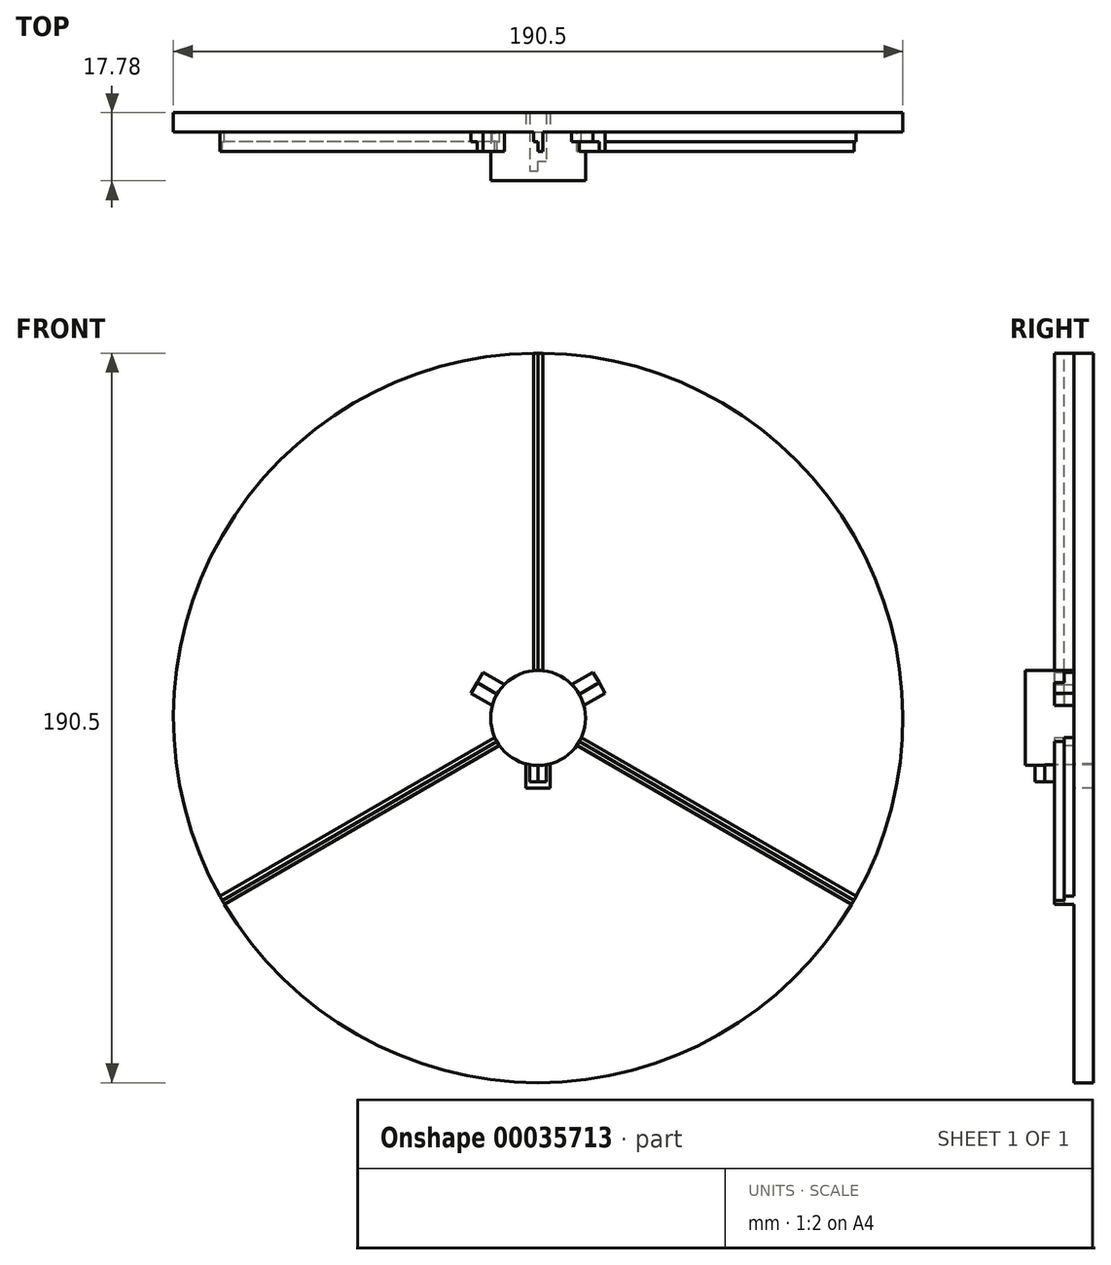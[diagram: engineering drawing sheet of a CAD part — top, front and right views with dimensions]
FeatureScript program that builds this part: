
annotation { "Feature Type Name" : "Feature", "Feature Type Description" : "" }
export const myFeature = defineFeature(function(context is Context, id is Id, definition is map)
    precondition{}
    {
        {
            var Q0;
            Q0=qCreatedBy(makeId("Front.planeOp"),FACE);
            var sketch = newSketch(context, id + "F0", { "sketchPlane" : qUnion([Q0])});
            skLineSegment(sketch, "E0.MirrorCS", {"start": v(1.2, 0) * mm, "end": v(1.2, 95.24) * mm});
            skLineSegment(sketch, "E1", {"start": v(0, 0) * mm, "end": v(-82.49, 47.62) * mm});
            skLineSegment(sketch, "E2", {"start": v(0, 0) * mm, "end": v(82.49, 47.62) * mm});
            skCircle(sketch, "E3", {"center": v(0, 0) * mm, "radius": 95.25 * mm});
            skLineSegment(sketch, "E4", {"start": v(0, 97.8) * mm, "end": v(-97.8, 97.8) * mm});
            skLineSegment(sketch, "E5", {"start": v(-97.8, -97.8) * mm, "end": v(0, -97.8) * mm});
            skLineSegment(sketch, "E6", {"start": v(-97.8, 97.8) * mm, "end": v(-97.8, -97.8) * mm});
            skLineSegment(sketch, "E7", {"start": v(0.6, 1.03) * mm, "end": v(83.08, -46.6) * mm});
            skLineSegment(sketch, "E8.MirrorCS", {"start": v(-0.6, -1.03) * mm, "end": v(81.89, -48.65) * mm});
            skLineSegment(sketch, "E9.MirrorCS", {"start": v(0, 97.8) * mm, "end": v(97.8, 97.8) * mm});
            skLineSegment(sketch, "E10.MirrorCS", {"start": v(97.8, -97.8) * mm, "end": v(0, -97.8) * mm});
            skLineSegment(sketch, "E11", {"start": v(-1.2, 0) * mm, "end": v(-1.2, 95.24) * mm});
            skLineSegment(sketch, "E12.MirrorCS", {"start": v(0, 0) * mm, "end": v(-82.49, -47.62) * mm});
            skLineSegment(sketch, "E13.MirrorCS", {"start": v(97.8, 97.8) * mm, "end": v(97.8, -97.8) * mm});
            skLineSegment(sketch, "E14.MirrorCS", {"start": v(-0.6, 1.03) * mm, "end": v(-83.08, -46.6) * mm});
            skLineSegment(sketch, "E15", {"start": v(0, 0) * mm, "end": v(0, -95.25) * mm});
            skLineSegment(sketch, "E16", {"start": v(0, 0) * mm, "end": v(0, 95.25) * mm});
            skLineSegment(sketch, "E17", {"start": v(0, 0) * mm, "end": v(82.49, -47.62) * mm});
            skLineSegment(sketch, "E18.MirrorCS", {"start": v(0.6, -1.03) * mm, "end": v(-81.89, -48.65) * mm});
            skCircle(sketch, "E19", {"center": v(0, 0) * mm, "radius": 12.4 * mm});
            skCircle(sketch, "E20", {"center": v(0, -15.21) * mm, "radius": 2.82 * mm, "construction": true});
            skLineSegment(sketch, "E21.MirrorCS", {"start": v(2.17, 0) * mm, "end": v(2.17, -14.57) * mm});
            skCircle(sketch, "E22", {"center": v(0, -14.57) * mm, "radius": 2.17 * mm, "construction": true});
            skLineSegment(sketch, "E23.MirrorCS", {"start": v(2.82, 0) * mm, "end": v(2.82, -15.21) * mm});
            skLineSegment(sketch, "E24", {"start": v(-2.17, 0) * mm, "end": v(-2.17, -14.57) * mm});
            skLineSegment(sketch, "E25", {"start": v(-2.82, 0) * mm, "end": v(-2.82, -15.21) * mm});
            skCircle(sketch, "E26", {"center": v(0, 0) * mm, "radius": 1.2 * mm, "construction": true});
            skLineSegment(sketch, "E27", {"start": v(-1.2, 0) * mm, "end": v(0, 0) * mm, "construction": true});
            skLineSegment(sketch, "E28", {"start": v(1.2, 0) * mm, "end": v(0, 0) * mm, "construction": true});
            skLineSegment(sketch, "E29.MirrorCS", {"start": v(-0.6, -1.03) * mm, "end": v(0, 0) * mm, "construction": true});
            skLineSegment(sketch, "E30.MirrorCS", {"start": v(0.6, 1.03) * mm, "end": v(0, 0) * mm, "construction": true});
            skLineSegment(sketch, "E31.MirrorCS", {"start": v(-0.6, 1.03) * mm, "end": v(0, 0) * mm, "construction": true});
            skLineSegment(sketch, "E32.MirrorCS", {"start": v(0.6, -1.03) * mm, "end": v(0, 0) * mm, "construction": true});
            skLineSegment(sketch, "E33", {"start": v(-2.82, 0) * mm, "end": v(0, 0) * mm, "construction": true});
            skLineSegment(sketch, "E34", {"start": v(0, 0) * mm, "end": v(2.82, 0) * mm, "construction": true});
            skLineSegment(sketch, "E35", {"start": v(-2.82, -15.21) * mm, "end": v(-2.82, -18.03) * mm});
            skLineSegment(sketch, "E36", {"start": v(-2.82, -18.03) * mm, "end": v(0, -18.03) * mm});
            skLineSegment(sketch, "E37", {"start": v(0, -18.03) * mm, "end": v(2.82, -18.03) * mm});
            skLineSegment(sketch, "E38", {"start": v(2.82, -18.03) * mm, "end": v(2.82, -15.21) * mm});
            skLineSegment(sketch, "E39", {"start": v(-2.17, -14.57) * mm, "end": v(-2.17, -16.74) * mm});
            skLineSegment(sketch, "E40", {"start": v(-2.17, -16.74) * mm, "end": v(0, -16.74) * mm});
            skLineSegment(sketch, "E41", {"start": v(0, -16.74) * mm, "end": v(2.17, -16.74) * mm});
            skLineSegment(sketch, "E42", {"start": v(2.17, -16.74) * mm, "end": v(2.17, -14.57) * mm});
            skCircle(sketch, "E43", {"center": v(-10.73, 6.2) * mm, "radius": 3.18 * mm, "construction": true});
            skCircle(sketch, "E44", {"center": v(0, -12.4) * mm, "radius": 3.18 * mm, "construction": true});
            skCircle(sketch, "E45", {"center": v(10.73, 6.2) * mm, "radius": 3.18 * mm, "construction": true});
            skLineSegment(sketch, "E46", {"start": v(-2.82, 0) * mm, "end": v(-3.18, 0) * mm, "construction": true});
            skLineSegment(sketch, "E47", {"start": v(-3.18, 0) * mm, "end": v(-3.18, -12.4) * mm});
            skLineSegment(sketch, "E48", {"start": v(-3.18, -12.4) * mm, "end": v(-3.18, -18.39) * mm});
            skLineSegment(sketch, "E49", {"start": v(-3.18, -18.39) * mm, "end": v(0, -18.39) * mm});
            skCircle(sketch, "E50", {"center": v(-2.82, -18.03) * mm, "radius": 0.36 * mm, "construction": true});
            skLineSegment(sketch, "E51.MirrorCS", {"start": v(2.82, 0) * mm, "end": v(3.17, 0) * mm});
            skLineSegment(sketch, "E52.MirrorCS", {"start": v(3.17, 0) * mm, "end": v(3.17, -12.4) * mm});
            skLineSegment(sketch, "E53.MirrorCS", {"start": v(3.17, -18.39) * mm, "end": v(0, -18.39) * mm});
            skLineSegment(sketch, "E54.MirrorCS", {"start": v(3.17, -12.4) * mm, "end": v(3.17, -18.39) * mm});
            skLineSegment(sketch, "E55.MirrorCS", {"start": v(1.4, -2.44) * mm, "end": v(1.59, -2.75) * mm, "construction": true});
            skLineSegment(sketch, "E56.MirrorCS", {"start": v(-1.4, 2.44) * mm, "end": v(-1.59, 2.75) * mm, "construction": true});
            skLineSegment(sketch, "E57.MirrorCS", {"start": v(-1.59, 2.75) * mm, "end": v(9.15, 8.95) * mm});
            skLineSegment(sketch, "E58.MirrorCS", {"start": v(1.59, -2.75) * mm, "end": v(12.32, 3.45) * mm});
            skLineSegment(sketch, "E59.MirrorCS", {"start": v(0, 0) * mm, "end": v(1.4, -2.44) * mm, "construction": true});
            skLineSegment(sketch, "E60.MirrorCS", {"start": v(-1.4, 2.44) * mm, "end": v(0, 0) * mm, "construction": true});
            skLineSegment(sketch, "E61.MirrorCS", {"start": v(9.15, 8.95) * mm, "end": v(14.34, 11.94) * mm});
            skLineSegment(sketch, "E62.MirrorCS", {"start": v(14.34, 11.94) * mm, "end": v(15.93, 9.2) * mm});
            skLineSegment(sketch, "E63.MirrorCS", {"start": v(12.32, 3.45) * mm, "end": v(17.51, 6.45) * mm});
            skLineSegment(sketch, "E64.MirrorCS", {"start": v(17.51, 6.45) * mm, "end": v(15.93, 9.2) * mm});
            skLineSegment(sketch, "E65.MirrorCS", {"start": v(1.4, 2.44) * mm, "end": v(1.59, 2.75) * mm, "construction": true});
            skLineSegment(sketch, "E66.MirrorCS", {"start": v(1.4, 2.44) * mm, "end": v(0, 0) * mm, "construction": true});
            skLineSegment(sketch, "E67.MirrorCS", {"start": v(1.59, 2.75) * mm, "end": v(-9.15, 8.95) * mm});
            skLineSegment(sketch, "E68.MirrorCS", {"start": v(0, 0) * mm, "end": v(-1.4, -2.44) * mm, "construction": true});
            skLineSegment(sketch, "E69.MirrorCS", {"start": v(-1.4, -2.44) * mm, "end": v(-1.59, -2.75) * mm, "construction": true});
            skLineSegment(sketch, "E70.MirrorCS", {"start": v(-1.59, -2.75) * mm, "end": v(-12.32, 3.45) * mm});
            skLineSegment(sketch, "E71.MirrorCS", {"start": v(-9.15, 8.95) * mm, "end": v(-14.34, 11.94) * mm});
            skLineSegment(sketch, "E72.MirrorCS", {"start": v(-14.34, 11.94) * mm, "end": v(-15.93, 9.2) * mm});
            skLineSegment(sketch, "E73.MirrorCS", {"start": v(-17.51, 6.45) * mm, "end": v(-15.93, 9.2) * mm});
            skLineSegment(sketch, "E74.MirrorCS", {"start": v(-12.32, 3.45) * mm, "end": v(-17.51, 6.45) * mm});
            skSolve(sketch);
        }
        {
            var Q0;
            {var subQ6=sQuery(id+"F0.wireOp",EDGE,"E61.MirrorCS");Q0=makeQuery(id+"F0.imprint","IMPRINT",FACE,{"disambiguationData":[TD([[makeQuery(id+"F0.imprint","IMPRINT",EDGE,{"derivedFrom":subQ6}),1.0]])]});}
            var Q1;
            {var subQ0=sQuery(id+"F0.wireOp",EDGE,"E71.MirrorCS");Q1=makeQuery(id+"F0.imprint","IMPRINT",FACE,{"disambiguationData":[TD([[makeQuery(id+"F0.imprint","IMPRINT",EDGE,{"derivedFrom":subQ0}),-1.0]])]});}
            var Q2;
            {var subQ1=sQuery(id+"F0.wireOp",EDGE,"E53.MirrorCS");Q2=makeQuery(id+"F0.imprint","IMPRINT",FACE,{"disambiguationData":[TD([[makeQuery(id+"F0.imprint","IMPRINT",EDGE,{"derivedFrom":subQ1}),1.0]])]});}
            var Q3;
            {var subQ0=sQuery(id+"F0.wireOp",EDGE,"E73.MirrorCS");Q3=makeQuery(id+"F0.imprint","IMPRINT",FACE,{"disambiguationData":[TD([[makeQuery(id+"F0.imprint","IMPRINT",EDGE,{"derivedFrom":subQ0}),1.0]])]});}
            var Q4;
            {var subQ1=sQuery(id+"F0.wireOp",EDGE,"E63.MirrorCS");Q4=makeQuery(id+"F0.imprint","IMPRINT",FACE,{"disambiguationData":[TD([[makeQuery(id+"F0.imprint","IMPRINT",EDGE,{"derivedFrom":subQ1}),-1.0]])]});}
            var Q5;
            {var subQ1=sQuery(id+"F0.wireOp",EDGE,"E48");Q5=makeQuery(id+"F0.imprint","IMPRINT",FACE,{"disambiguationData":[TD([[makeQuery(id+"F0.imprint","IMPRINT",EDGE,{"derivedFrom":subQ1}),-1.0]])]});}
            var Q6;
            Q6=makeQuery(id+"F0.imprint","IMPRINT",FACE,{"disambiguationData":[TD([[makeQuery(id+"F0.imprint","IMPRINT",EDGE,{"derivedFrom":sQuery(id+"F0.wireOp",EDGE,"E4")}),1.0]])]});
            var Q7;
            {var subQ3=sQuery(id+"F0.wireOp",EDGE,"E0.MirrorCS");var subQ5=sQuery(id+"F0.wireOp",EDGE,"E3");var subQ7=makeQuery(id+"F0.imprint","INTERSECT",VERTEX,{"derivedFrom":[subQ3,subQ5]});Q7=makeQuery(id+"F0.imprint","IMPRINT",FACE,{"disambiguationData":[TD([[makeQuery(id+"F0.imprint","IMPRINT",EDGE,{"disambiguationData":[TD([[subQ7,1.0]])],"derivedFrom":subQ3}),1.0]])]});}
            var Q8;
            {var subQ3=sQuery(id+"F0.wireOp",EDGE,"E8.MirrorCS");var subQ5=sQuery(id+"F0.wireOp",EDGE,"E3");var subQ7=makeQuery(id+"F0.imprint","INTERSECT",VERTEX,{"derivedFrom":[subQ5,subQ3]});Q8=makeQuery(id+"F0.imprint","IMPRINT",FACE,{"disambiguationData":[TD([[makeQuery(id+"F0.imprint","IMPRINT",EDGE,{"disambiguationData":[TD([[subQ7,-1.0]])],"derivedFrom":subQ5}),1.0]])]});}
            var Q9;
            {var subQ3=sQuery(id+"F0.wireOp",EDGE,"E3");var subQ5=sQuery(id+"F0.wireOp",EDGE,"E12.MirrorCS");var subQ7=makeQuery(id+"F0.imprint","INTERSECT",VERTEX,{"derivedFrom":[subQ3,subQ5]});Q9=makeQuery(id+"F0.imprint","IMPRINT",FACE,{"disambiguationData":[TD([[makeQuery(id+"F0.imprint","IMPRINT",EDGE,{"disambiguationData":[TD([[subQ7,-1.0]])],"derivedFrom":subQ3}),1.0]])]});}
            var Q10;
            {var subQ3=sQuery(id+"F0.wireOp",EDGE,"E11");var subQ5=sQuery(id+"F0.wireOp",EDGE,"E3");var subQ7=makeQuery(id+"F0.imprint","INTERSECT",VERTEX,{"derivedFrom":[subQ5,subQ3]});Q10=makeQuery(id+"F0.imprint","IMPRINT",FACE,{"disambiguationData":[TD([[makeQuery(id+"F0.imprint","IMPRINT",EDGE,{"disambiguationData":[TD([[subQ7,1.0]])],"derivedFrom":subQ5}),1.0]])]});}
            var Q11;
            {var subQ3=sQuery(id+"F0.wireOp",EDGE,"E12.MirrorCS");var subQ5=sQuery(id+"F0.wireOp",EDGE,"E3");var subQ7=makeQuery(id+"F0.imprint","INTERSECT",VERTEX,{"derivedFrom":[subQ5,subQ3]});Q11=makeQuery(id+"F0.imprint","IMPRINT",FACE,{"disambiguationData":[TD([[makeQuery(id+"F0.imprint","IMPRINT",EDGE,{"disambiguationData":[TD([[subQ7,1.0]])],"derivedFrom":subQ5}),1.0]])]});}
            var Q12;
            {var subQ3=sQuery(id+"F0.wireOp",EDGE,"E7");var subQ5=sQuery(id+"F0.wireOp",EDGE,"E3");var subQ7=makeQuery(id+"F0.imprint","INTERSECT",VERTEX,{"derivedFrom":[subQ5,subQ3]});Q12=makeQuery(id+"F0.imprint","IMPRINT",FACE,{"disambiguationData":[TD([[makeQuery(id+"F0.imprint","IMPRINT",EDGE,{"disambiguationData":[TD([[subQ7,1.0]])],"derivedFrom":subQ5}),1.0]])]});}
            var Q13;
            {var subQ0=sQuery(id+"F0.wireOp",EDGE,"E57.MirrorCS");var subQ3=sQuery(id+"F0.wireOp",EDGE,"E0.MirrorCS");var subQ4=makeQuery(id+"F0.imprint","INTERSECT",VERTEX,{"derivedFrom":[subQ3,subQ0]});Q13=makeQuery(id+"F0.imprint","IMPRINT",FACE,{"disambiguationData":[TD([[makeQuery(id+"F0.imprint","IMPRINT",EDGE,{"disambiguationData":[TD([[subQ4,-1.0]])],"derivedFrom":subQ3}),-1.0]])]});}
            var Q14;
            {var subQ0=sQuery(id+"F0.wireOp",EDGE,"E67.MirrorCS");var subQ3=sQuery(id+"F0.wireOp",EDGE,"E11");var subQ4=makeQuery(id+"F0.imprint","INTERSECT",VERTEX,{"derivedFrom":[subQ3,subQ0]});Q14=makeQuery(id+"F0.imprint","IMPRINT",FACE,{"disambiguationData":[TD([[makeQuery(id+"F0.imprint","IMPRINT",EDGE,{"disambiguationData":[TD([[subQ4,-1.0]])],"derivedFrom":subQ3}),1.0]])]});}
            var Q15;
            {var subQ0=sQuery(id+"F0.wireOp",EDGE,"E57.MirrorCS");var subQ3=sQuery(id+"F0.wireOp",EDGE,"E0.MirrorCS");var subQ4=makeQuery(id+"F0.imprint","INTERSECT",VERTEX,{"derivedFrom":[subQ3,subQ0]});Q15=makeQuery(id+"F0.imprint","IMPRINT",FACE,{"disambiguationData":[TD([[makeQuery(id+"F0.imprint","IMPRINT",EDGE,{"disambiguationData":[TD([[subQ4,-1.0]])],"derivedFrom":subQ3}),1.0]])]});}
            var Q16;
            {var subQ0=sQuery(id+"F0.wireOp",EDGE,"E47");var subQ3=sQuery(id+"F0.wireOp",EDGE,"E18.MirrorCS");var subQ4=makeQuery(id+"F0.imprint","INTERSECT",VERTEX,{"derivedFrom":[subQ3,subQ0]});Q16=makeQuery(id+"F0.imprint","IMPRINT",FACE,{"disambiguationData":[TD([[makeQuery(id+"F0.imprint","IMPRINT",EDGE,{"disambiguationData":[TD([[subQ4,-1.0]])],"derivedFrom":subQ3}),1.0]])]});}
            var Q17;
            {var subQ6=sQuery(id+"F0.wireOp",EDGE,"E61.MirrorCS");Q17=makeQuery(id+"F0.imprint","IMPRINT",FACE,{"disambiguationData":[TD([[makeQuery(id+"F0.imprint","IMPRINT",EDGE,{"derivedFrom":subQ6}),-1.0]])]});}
            var Q18;
            {var subQ1=sQuery(id+"F0.wireOp",EDGE,"E52.MirrorCS");var subQ3=sQuery(id+"F0.wireOp",EDGE,"E8.MirrorCS");var subQ5=makeQuery(id+"F0.imprint","INTERSECT",VERTEX,{"derivedFrom":[subQ3,subQ1]});Q18=makeQuery(id+"F0.imprint","IMPRINT",FACE,{"disambiguationData":[TD([[makeQuery(id+"F0.imprint","IMPRINT",EDGE,{"disambiguationData":[TD([[subQ5,-1.0]])],"derivedFrom":subQ3}),-1.0]])]});}
            var Q19;
            {var subQ6=sQuery(id+"F0.wireOp",EDGE,"E71.MirrorCS");Q19=makeQuery(id+"F0.imprint","IMPRINT",FACE,{"disambiguationData":[TD([[makeQuery(id+"F0.imprint","IMPRINT",EDGE,{"derivedFrom":subQ6}),1.0]])]});}
            var Q20;
            {var subQ0=sQuery(id+"F0.wireOp",EDGE,"E67.MirrorCS");var subQ3=sQuery(id+"F0.wireOp",EDGE,"E11");var subQ4=makeQuery(id+"F0.imprint","INTERSECT",VERTEX,{"derivedFrom":[subQ3,subQ0]});Q20=makeQuery(id+"F0.imprint","IMPRINT",FACE,{"disambiguationData":[TD([[makeQuery(id+"F0.imprint","IMPRINT",EDGE,{"disambiguationData":[TD([[subQ4,-1.0]])],"derivedFrom":subQ3}),-1.0]])]});}
            var Q21;
            {var subQ0=sQuery(id+"F0.wireOp",EDGE,"E58.MirrorCS");var subQ3=sQuery(id+"F0.wireOp",EDGE,"E7");var subQ4=makeQuery(id+"F0.imprint","INTERSECT",VERTEX,{"derivedFrom":[subQ3,subQ0]});Q21=makeQuery(id+"F0.imprint","IMPRINT",FACE,{"disambiguationData":[TD([[makeQuery(id+"F0.imprint","IMPRINT",EDGE,{"disambiguationData":[TD([[subQ4,-1.0]])],"derivedFrom":subQ3}),-1.0]])]});}
            var Q22;
            {var subQ3=sQuery(id+"F0.wireOp",EDGE,"E11");var subQ8=makeQuery(id+"F0.imprint","INTERSECT",VERTEX,{"derivedFrom":[subQ3,sQuery(id+"F0.wireOp",EDGE,"E57.MirrorCS")]});Q22=makeQuery(id+"F0.imprint","IMPRINT",FACE,{"disambiguationData":[TD([[makeQuery(id+"F0.imprint","IMPRINT",EDGE,{"disambiguationData":[TD([[subQ8,-1.0]])],"derivedFrom":subQ3}),1.0]])]});}
            var Q23;
            {var subQ3=sQuery(id+"F0.wireOp",EDGE,"E18.MirrorCS");var subQ7=makeQuery(id+"F0.imprint","INTERSECT",VERTEX,{"derivedFrom":[subQ3,sQuery(id+"F0.wireOp",EDGE,"E70.MirrorCS")]});Q23=makeQuery(id+"F0.imprint","IMPRINT",FACE,{"disambiguationData":[TD([[makeQuery(id+"F0.imprint","IMPRINT",EDGE,{"disambiguationData":[TD([[subQ7,-1.0]])],"derivedFrom":subQ3}),1.0]])]});}
            var Q24;
            {var subQ3=sQuery(id+"F0.wireOp",EDGE,"E73.MirrorCS");Q24=makeQuery(id+"F0.imprint","IMPRINT",FACE,{"disambiguationData":[TD([[makeQuery(id+"F0.imprint","IMPRINT",EDGE,{"derivedFrom":subQ3}),-1.0]])]});}
            var Q25;
            {var subQ3=sQuery(id+"F0.wireOp",EDGE,"E0.MirrorCS");var subQ5=makeQuery(id+"F0.imprint","INTERSECT",VERTEX,{"derivedFrom":[subQ3,sQuery(id+"F0.wireOp",EDGE,"E67.MirrorCS")]});Q25=makeQuery(id+"F0.imprint","IMPRINT",FACE,{"disambiguationData":[TD([[makeQuery(id+"F0.imprint","IMPRINT",EDGE,{"disambiguationData":[TD([[subQ5,-1.0]])],"derivedFrom":subQ3}),-1.0]])]});}
            var Q26;
            {var subQ3=sQuery(id+"F0.wireOp",EDGE,"E8.MirrorCS");var subQ5=sQuery(id+"F0.wireOp",EDGE,"E52.MirrorCS");var subQ7=makeQuery(id+"F0.imprint","INTERSECT",VERTEX,{"derivedFrom":[subQ3,subQ5]});Q26=makeQuery(id+"F0.imprint","IMPRINT",FACE,{"disambiguationData":[TD([[makeQuery(id+"F0.imprint","IMPRINT",EDGE,{"disambiguationData":[TD([[subQ7,-1.0]])],"derivedFrom":subQ3}),1.0]])]});}
            var Q27;
            {var subQ3=sQuery(id+"F0.wireOp",EDGE,"E14.MirrorCS");var subQ8=makeQuery(id+"F0.imprint","INTERSECT",VERTEX,{"derivedFrom":[subQ3,sQuery(id+"F0.wireOp",EDGE,"E25")]});Q27=makeQuery(id+"F0.imprint","IMPRINT",FACE,{"disambiguationData":[TD([[makeQuery(id+"F0.imprint","IMPRINT",EDGE,{"disambiguationData":[TD([[subQ8,-1.0]])],"derivedFrom":subQ3}),-1.0]])]});}
            var Q28;
            {var subQ6=sQuery(id+"F0.wireOp",EDGE,"E63.MirrorCS");Q28=makeQuery(id+"F0.imprint","IMPRINT",FACE,{"disambiguationData":[TD([[makeQuery(id+"F0.imprint","IMPRINT",EDGE,{"derivedFrom":subQ6}),1.0]])]});}
            var Q29;
            {var subQ0=sQuery(id+"F0.wireOp",EDGE,"E67.MirrorCS");var subQ3=sQuery(id+"F0.wireOp",EDGE,"E0.MirrorCS");var subQ4=makeQuery(id+"F0.imprint","INTERSECT",VERTEX,{"derivedFrom":[subQ3,subQ0]});Q29=makeQuery(id+"F0.imprint","IMPRINT",FACE,{"disambiguationData":[TD([[makeQuery(id+"F0.imprint","IMPRINT",EDGE,{"disambiguationData":[TD([[subQ4,-1.0]])],"derivedFrom":subQ3}),1.0]])]});}
            var Q30;
            {var subQ0=sQuery(id+"F0.wireOp",EDGE,"E23.MirrorCS");var subQ3=sQuery(id+"F0.wireOp",EDGE,"E8.MirrorCS");var subQ4=makeQuery(id+"F0.imprint","INTERSECT",VERTEX,{"derivedFrom":[subQ3,subQ0]});Q30=makeQuery(id+"F0.imprint","IMPRINT",FACE,{"disambiguationData":[TD([[makeQuery(id+"F0.imprint","IMPRINT",EDGE,{"disambiguationData":[TD([[subQ4,-1.0]])],"derivedFrom":subQ3}),-1.0]])]});}
            var Q31;
            {var subQ0=sQuery(id+"F0.wireOp",EDGE,"E24");var subQ3=sQuery(id+"F0.wireOp",EDGE,"E18.MirrorCS");var subQ4=makeQuery(id+"F0.imprint","INTERSECT",VERTEX,{"derivedFrom":[subQ3,subQ0]});Q31=makeQuery(id+"F0.imprint","IMPRINT",FACE,{"disambiguationData":[TD([[makeQuery(id+"F0.imprint","IMPRINT",EDGE,{"disambiguationData":[TD([[subQ4,-1.0]])],"derivedFrom":subQ3}),1.0]])]});}
            var Q32;
            {var subQ3=sQuery(id+"F0.wireOp",EDGE,"E18.MirrorCS");var subQ5=sQuery(id+"F0.wireOp",EDGE,"E25");var subQ7=makeQuery(id+"F0.imprint","INTERSECT",VERTEX,{"derivedFrom":[subQ3,subQ5]});Q32=makeQuery(id+"F0.imprint","IMPRINT",FACE,{"disambiguationData":[TD([[makeQuery(id+"F0.imprint","IMPRINT",EDGE,{"disambiguationData":[TD([[subQ7,-1.0]])],"derivedFrom":subQ3}),1.0]])]});}
            var Q33;
            {var subQ3=sQuery(id+"F0.wireOp",EDGE,"E8.MirrorCS");var subQ5=sQuery(id+"F0.wireOp",EDGE,"E21.MirrorCS");var subQ7=makeQuery(id+"F0.imprint","INTERSECT",VERTEX,{"derivedFrom":[subQ3,subQ5]});Q33=makeQuery(id+"F0.imprint","IMPRINT",FACE,{"disambiguationData":[TD([[makeQuery(id+"F0.imprint","IMPRINT",EDGE,{"disambiguationData":[TD([[subQ7,-1.0]])],"derivedFrom":subQ3}),-1.0]])]});}
            var Q34;
            {var subQ0=sQuery(id+"F0.wireOp",EDGE,"E70.MirrorCS");var subQ3=sQuery(id+"F0.wireOp",EDGE,"E14.MirrorCS");var subQ4=makeQuery(id+"F0.imprint","INTERSECT",VERTEX,{"derivedFrom":[subQ3,subQ0]});Q34=makeQuery(id+"F0.imprint","IMPRINT",FACE,{"disambiguationData":[TD([[makeQuery(id+"F0.imprint","IMPRINT",EDGE,{"disambiguationData":[TD([[subQ4,-1.0]])],"derivedFrom":subQ3}),-1.0]])]});}
            var Q35;
            {var subQ3=sQuery(id+"F0.wireOp",EDGE,"E8.MirrorCS");var subQ5=makeQuery(id+"F0.imprint","INTERSECT",VERTEX,{"derivedFrom":[subQ3,sQuery(id+"F0.wireOp",EDGE,"E58.MirrorCS")]});Q35=makeQuery(id+"F0.imprint","IMPRINT",FACE,{"disambiguationData":[TD([[makeQuery(id+"F0.imprint","IMPRINT",EDGE,{"disambiguationData":[TD([[subQ5,-1.0]])],"derivedFrom":subQ3}),-1.0]])]});}
            var Q36;
            {var subQ1=sQuery(id+"F0.wireOp",EDGE,"E14.MirrorCS");var subQ5=sQuery(id+"F0.wireOp",EDGE,"E70.MirrorCS");var subQ6=makeQuery(id+"F0.imprint","INTERSECT",VERTEX,{"derivedFrom":[subQ1,subQ5]});Q36=makeQuery(id+"F0.imprint","IMPRINT",FACE,{"disambiguationData":[TD([[makeQuery(id+"F0.imprint","IMPRINT",EDGE,{"disambiguationData":[TD([[subQ6,-1.0]])],"derivedFrom":subQ1}),1.0]])]});}
            var Q37;
            {var subQ4=sQuery(id+"F0.wireOp",EDGE,"E41");Q37=makeQuery(id+"F0.imprint","IMPRINT",FACE,{"disambiguationData":[TD([[makeQuery(id+"F0.imprint","IMPRINT",EDGE,{"derivedFrom":subQ4}),1.0]])]});}
            var Q38;
            {var subQ6=sQuery(id+"F0.wireOp",EDGE,"E37");Q38=makeQuery(id+"F0.imprint","IMPRINT",FACE,{"disambiguationData":[TD([[makeQuery(id+"F0.imprint","IMPRINT",EDGE,{"derivedFrom":subQ6}),-1.0]])]});}
            var Q39;
            {var subQ4=sQuery(id+"F0.wireOp",EDGE,"E37");Q39=makeQuery(id+"F0.imprint","IMPRINT",FACE,{"disambiguationData":[TD([[makeQuery(id+"F0.imprint","IMPRINT",EDGE,{"derivedFrom":subQ4}),1.0]])]});}
            var Q40;
            {var subQ6=sQuery(id+"F0.wireOp",EDGE,"E39");Q40=makeQuery(id+"F0.imprint","IMPRINT",FACE,{"disambiguationData":[TD([[makeQuery(id+"F0.imprint","IMPRINT",EDGE,{"derivedFrom":subQ6}),1.0]])]});}
            var Q41;
            {var subQ9=sQuery(id+"F0.wireOp",EDGE,"E35");Q41=makeQuery(id+"F0.imprint","IMPRINT",FACE,{"disambiguationData":[TD([[makeQuery(id+"F0.imprint","IMPRINT",EDGE,{"derivedFrom":subQ9}),-1.0]])]});}
            var Q42;
            {var subQ0=sQuery(id+"F0.wireOp",EDGE,"E35");Q42=makeQuery(id+"F0.imprint","IMPRINT",FACE,{"disambiguationData":[TD([[makeQuery(id+"F0.imprint","IMPRINT",EDGE,{"derivedFrom":subQ0}),1.0]])]});}
            var Q43;
            {var subQ0=sQuery(id+"F0.wireOp",EDGE,"E58.MirrorCS");var subQ3=sQuery(id+"F0.wireOp",EDGE,"E7");var subQ4=makeQuery(id+"F0.imprint","INTERSECT",VERTEX,{"derivedFrom":[subQ3,subQ0]});Q43=makeQuery(id+"F0.imprint","IMPRINT",FACE,{"disambiguationData":[TD([[makeQuery(id+"F0.imprint","IMPRINT",EDGE,{"disambiguationData":[TD([[subQ4,-1.0]])],"derivedFrom":subQ3}),1.0]])]});}
            var Q44;
            {var subQ5=sQuery(id+"F0.wireOp",EDGE,"E51.MirrorCS");Q44=makeQuery(id+"F0.imprint","IMPRINT",FACE,{"disambiguationData":[TD([[makeQuery(id+"F0.imprint","IMPRINT",EDGE,{"derivedFrom":subQ5}),1.0]])]});}
            var Q45;
            {var subQ0=sQuery(id+"F0.wireOp",EDGE,"E47");var subQ3=sQuery(id+"F0.wireOp",EDGE,"E18.MirrorCS");var subQ4=makeQuery(id+"F0.imprint","INTERSECT",VERTEX,{"derivedFrom":[subQ3,subQ0]});Q45=makeQuery(id+"F0.imprint","IMPRINT",FACE,{"disambiguationData":[TD([[makeQuery(id+"F0.imprint","IMPRINT",EDGE,{"disambiguationData":[TD([[subQ4,-1.0]])],"derivedFrom":subQ3}),-1.0]])]});}
            var Q46;
            {var subQ0=sQuery(id+"F0.wireOp",EDGE,"E67.MirrorCS");var subQ3=sQuery(id+"F0.wireOp",EDGE,"E0.MirrorCS");var subQ4=makeQuery(id+"F0.imprint","INTERSECT",VERTEX,{"derivedFrom":[subQ3,subQ0]});Q46=makeQuery(id+"F0.imprint","IMPRINT",FACE,{"disambiguationData":[TD([[makeQuery(id+"F0.imprint","IMPRINT",EDGE,{"disambiguationData":[TD([[subQ4,1.0]])],"derivedFrom":subQ3}),1.0]])]});}
            var Q47;
            {var subQ3=sQuery(id+"F0.wireOp",EDGE,"E21.MirrorCS");var subQ5=sQuery(id+"F0.wireOp",EDGE,"E8.MirrorCS");var subQ7=makeQuery(id+"F0.imprint","INTERSECT",VERTEX,{"derivedFrom":[subQ5,subQ3]});Q47=makeQuery(id+"F0.imprint","IMPRINT",FACE,{"disambiguationData":[TD([[makeQuery(id+"F0.imprint","IMPRINT",EDGE,{"disambiguationData":[TD([[subQ7,-1.0]])],"derivedFrom":subQ5}),1.0]])]});}
            var Q48;
            {var subQ0=sQuery(id+"F0.wireOp",EDGE,"E57.MirrorCS");var subQ3=sQuery(id+"F0.wireOp",EDGE,"E11");var subQ4=makeQuery(id+"F0.imprint","INTERSECT",VERTEX,{"derivedFrom":[subQ3,subQ0]});Q48=makeQuery(id+"F0.imprint","IMPRINT",FACE,{"disambiguationData":[TD([[makeQuery(id+"F0.imprint","IMPRINT",EDGE,{"disambiguationData":[TD([[subQ4,1.0]])],"derivedFrom":subQ3}),-1.0]])]});}
            var Q49;
            {var subQ1=sQuery(id+"F0.wireOp",EDGE,"E24");var subQ7=sQuery(id+"F0.wireOp",EDGE,"E12.MirrorCS");var subQ9=makeQuery(id+"F0.imprint","INTERSECT",VERTEX,{"derivedFrom":[subQ7,subQ1]});Q49=makeQuery(id+"F0.imprint","IMPRINT",FACE,{"disambiguationData":[TD([[makeQuery(id+"F0.imprint","IMPRINT",EDGE,{"disambiguationData":[TD([[subQ9,-1.0]])],"derivedFrom":subQ1}),1.0]])]});}
            var Q50;
            {var subQ5=sQuery(id+"F0.wireOp",EDGE,"E17");var subQ7=sQuery(id+"F0.wireOp",EDGE,"E21.MirrorCS");var subQ8=makeQuery(id+"F0.imprint","INTERSECT",VERTEX,{"derivedFrom":[subQ5,subQ7]});Q50=makeQuery(id+"F0.imprint","IMPRINT",FACE,{"disambiguationData":[TD([[makeQuery(id+"F0.imprint","IMPRINT",EDGE,{"disambiguationData":[TD([[subQ8,-1.0]])],"derivedFrom":subQ7}),-1.0]])]});}
            var Q51;
            {var subQ3=sQuery(id+"F0.wireOp",EDGE,"E23.MirrorCS");var subQ5=sQuery(id+"F0.wireOp",EDGE,"E8.MirrorCS");var subQ6=makeQuery(id+"F0.imprint","INTERSECT",VERTEX,{"derivedFrom":[subQ5,subQ3]});Q51=makeQuery(id+"F0.imprint","IMPRINT",FACE,{"disambiguationData":[TD([[makeQuery(id+"F0.imprint","IMPRINT",EDGE,{"disambiguationData":[TD([[subQ6,-1.0]])],"derivedFrom":subQ5}),1.0]])]});}
            var Q52;
            {var subQ3=sQuery(id+"F0.wireOp",EDGE,"E24");var subQ5=sQuery(id+"F0.wireOp",EDGE,"E18.MirrorCS");var subQ6=makeQuery(id+"F0.imprint","INTERSECT",VERTEX,{"derivedFrom":[subQ5,subQ3]});Q52=makeQuery(id+"F0.imprint","IMPRINT",FACE,{"disambiguationData":[TD([[makeQuery(id+"F0.imprint","IMPRINT",EDGE,{"disambiguationData":[TD([[subQ6,-1.0]])],"derivedFrom":subQ5}),-1.0]])]});}
            var Q53;
            {var subQ3=sQuery(id+"F0.wireOp",EDGE,"E7");var subQ5=sQuery(id+"F0.wireOp",EDGE,"E23.MirrorCS");var subQ7=makeQuery(id+"F0.imprint","INTERSECT",VERTEX,{"derivedFrom":[subQ3,subQ5]});Q53=makeQuery(id+"F0.imprint","IMPRINT",FACE,{"disambiguationData":[TD([[makeQuery(id+"F0.imprint","IMPRINT",EDGE,{"disambiguationData":[TD([[subQ7,-1.0]])],"derivedFrom":subQ3}),-1.0]])]});}
            var Q54;
            {var subQ3=sQuery(id+"F0.wireOp",EDGE,"E21.MirrorCS");var subQ5=sQuery(id+"F0.wireOp",EDGE,"E17");var subQ7=makeQuery(id+"F0.imprint","INTERSECT",VERTEX,{"derivedFrom":[subQ5,subQ3]});Q54=makeQuery(id+"F0.imprint","IMPRINT",FACE,{"disambiguationData":[TD([[makeQuery(id+"F0.imprint","IMPRINT",EDGE,{"disambiguationData":[TD([[subQ7,-1.0]])],"derivedFrom":subQ5}),-1.0]])]});}
            var Q55;
            {var subQ3=sQuery(id+"F0.wireOp",EDGE,"E24");var subQ5=sQuery(id+"F0.wireOp",EDGE,"E12.MirrorCS");var subQ7=makeQuery(id+"F0.imprint","INTERSECT",VERTEX,{"derivedFrom":[subQ5,subQ3]});Q55=makeQuery(id+"F0.imprint","IMPRINT",FACE,{"disambiguationData":[TD([[makeQuery(id+"F0.imprint","IMPRINT",EDGE,{"disambiguationData":[TD([[subQ7,-1.0]])],"derivedFrom":subQ5}),1.0]])]});}
            var Q56;
            {var subQ3=sQuery(id+"F0.wireOp",EDGE,"E25");var subQ5=sQuery(id+"F0.wireOp",EDGE,"E18.MirrorCS");var subQ7=makeQuery(id+"F0.imprint","INTERSECT",VERTEX,{"derivedFrom":[subQ5,subQ3]});Q56=makeQuery(id+"F0.imprint","IMPRINT",FACE,{"disambiguationData":[TD([[makeQuery(id+"F0.imprint","IMPRINT",EDGE,{"disambiguationData":[TD([[subQ7,-1.0]])],"derivedFrom":subQ5}),-1.0]])]});}
            var Q57;
            {var subQ1=sQuery(id+"F0.wireOp",EDGE,"E17");var subQ8=makeQuery(id+"F0.imprint","INTERSECT",VERTEX,{"derivedFrom":[subQ1,sQuery(id+"F0.wireOp",EDGE,"E21.MirrorCS")]});Q57=makeQuery(id+"F0.imprint","IMPRINT",FACE,{"disambiguationData":[TD([[makeQuery(id+"F0.imprint","IMPRINT",EDGE,{"disambiguationData":[TD([[subQ8,-1.0]])],"derivedFrom":subQ1}),1.0]])]});}
            var Q58;
            {var subQ1=sQuery(id+"F0.wireOp",EDGE,"E12.MirrorCS");var subQ8=makeQuery(id+"F0.imprint","INTERSECT",VERTEX,{"derivedFrom":[subQ1,sQuery(id+"F0.wireOp",EDGE,"E24")]});Q58=makeQuery(id+"F0.imprint","IMPRINT",FACE,{"disambiguationData":[TD([[makeQuery(id+"F0.imprint","IMPRINT",EDGE,{"disambiguationData":[TD([[subQ8,-1.0]])],"derivedFrom":subQ1}),-1.0]])]});}
            var Q59;
            {var subQ1=sQuery(id+"F0.wireOp",EDGE,"E57.MirrorCS");var subQ3=sQuery(id+"F0.wireOp",EDGE,"E11");var subQ5=makeQuery(id+"F0.imprint","INTERSECT",VERTEX,{"derivedFrom":[subQ3,subQ1]});Q59=makeQuery(id+"F0.imprint","IMPRINT",FACE,{"disambiguationData":[TD([[makeQuery(id+"F0.imprint","IMPRINT",EDGE,{"disambiguationData":[TD([[subQ5,-1.0]])],"derivedFrom":subQ3}),-1.0]])]});}
            var Q60;
            {var subQ1=sQuery(id+"F0.wireOp",EDGE,"E47");var subQ3=sQuery(id+"F0.wireOp",EDGE,"E14.MirrorCS");var subQ5=makeQuery(id+"F0.imprint","INTERSECT",VERTEX,{"derivedFrom":[subQ3,subQ1]});Q60=makeQuery(id+"F0.imprint","IMPRINT",FACE,{"disambiguationData":[TD([[makeQuery(id+"F0.imprint","IMPRINT",EDGE,{"disambiguationData":[TD([[subQ5,-1.0]])],"derivedFrom":subQ3}),1.0]])]});}
            var Q61;
            {var subQ0=sQuery(id+"F0.wireOp",EDGE,"E25");var subQ3=sQuery(id+"F0.wireOp",EDGE,"E14.MirrorCS");var subQ4=makeQuery(id+"F0.imprint","INTERSECT",VERTEX,{"derivedFrom":[subQ3,subQ0]});Q61=makeQuery(id+"F0.imprint","IMPRINT",FACE,{"disambiguationData":[TD([[makeQuery(id+"F0.imprint","IMPRINT",EDGE,{"disambiguationData":[TD([[subQ4,-1.0]])],"derivedFrom":subQ3}),1.0]])]});}
            var Q62;
            {var subQ1=sQuery(id+"F0.wireOp",EDGE,"E12.MirrorCS");var subQ3=sQuery(id+"F0.wireOp",EDGE,"E25");var subQ5=makeQuery(id+"F0.imprint","INTERSECT",VERTEX,{"derivedFrom":[subQ1,subQ3]});Q62=makeQuery(id+"F0.imprint","IMPRINT",FACE,{"disambiguationData":[TD([[makeQuery(id+"F0.imprint","IMPRINT",EDGE,{"disambiguationData":[TD([[subQ5,-1.0]])],"derivedFrom":subQ3}),-1.0]])]});}
            var Q63;
            {var subQ0=sQuery(id+"F0.wireOp",EDGE,"E70.MirrorCS");var subQ3=sQuery(id+"F0.wireOp",EDGE,"E18.MirrorCS");var subQ4=makeQuery(id+"F0.imprint","INTERSECT",VERTEX,{"derivedFrom":[subQ3,subQ0]});Q63=makeQuery(id+"F0.imprint","IMPRINT",FACE,{"disambiguationData":[TD([[makeQuery(id+"F0.imprint","IMPRINT",EDGE,{"disambiguationData":[TD([[subQ4,-1.0]])],"derivedFrom":subQ3}),-1.0]])]});}
            var Q64;
            {var subQ0=sQuery(id+"F0.wireOp",EDGE,"E58.MirrorCS");var subQ3=sQuery(id+"F0.wireOp",EDGE,"E8.MirrorCS");var subQ4=makeQuery(id+"F0.imprint","INTERSECT",VERTEX,{"derivedFrom":[subQ3,subQ0]});Q64=makeQuery(id+"F0.imprint","IMPRINT",FACE,{"disambiguationData":[TD([[makeQuery(id+"F0.imprint","IMPRINT",EDGE,{"disambiguationData":[TD([[subQ4,-1.0]])],"derivedFrom":subQ3}),1.0]])]});}
            var Q65;
            {var subQ1=sQuery(id+"F0.wireOp",EDGE,"E17");var subQ3=sQuery(id+"F0.wireOp",EDGE,"E23.MirrorCS");var subQ5=makeQuery(id+"F0.imprint","INTERSECT",VERTEX,{"derivedFrom":[subQ1,subQ3]});Q65=makeQuery(id+"F0.imprint","IMPRINT",FACE,{"disambiguationData":[TD([[makeQuery(id+"F0.imprint","IMPRINT",EDGE,{"disambiguationData":[TD([[subQ5,-1.0]])],"derivedFrom":subQ3}),1.0]])]});}
            var Q66;
            {var subQ1=sQuery(id+"F0.wireOp",EDGE,"E52.MirrorCS");var subQ3=sQuery(id+"F0.wireOp",EDGE,"E7");var subQ5=makeQuery(id+"F0.imprint","INTERSECT",VERTEX,{"derivedFrom":[subQ3,subQ1]});Q66=makeQuery(id+"F0.imprint","IMPRINT",FACE,{"disambiguationData":[TD([[makeQuery(id+"F0.imprint","IMPRINT",EDGE,{"disambiguationData":[TD([[subQ5,-1.0]])],"derivedFrom":subQ3}),-1.0]])]});}
            var Q67;
            {var subQ3=sQuery(id+"F0.wireOp",EDGE,"E51.MirrorCS");Q67=makeQuery(id+"F0.imprint","IMPRINT",FACE,{"disambiguationData":[TD([[makeQuery(id+"F0.imprint","IMPRINT",EDGE,{"derivedFrom":subQ3}),-1.0]])]});}
            extrude(context, id + "F1", {"entities" : qUnion([Q0, Q1, Q2, Q3, Q4, Q5, Q6, Q7, Q8, Q9, Q10, Q11, Q12, Q13, Q14, Q15, Q16, Q17, Q18, Q19, Q20, Q21, Q22, Q23, Q24, Q25, Q26, Q27, Q28, Q29, Q30, Q31, Q32, Q33, Q34, Q35, Q36, Q37, Q38, Q39, Q40, Q41, Q42, Q43, Q44, Q45, Q46, Q47, Q48, Q49, Q50, Q51, Q52, Q53, Q54, Q55, Q56, Q57, Q58, Q59, Q60, Q61, Q62, Q63, Q64, Q65, Q66, Q67]), "oppositeDirection" : true, "depth" : 2.54 * mm});
        }
        {
            var Q0;
            {var subQ0=sQuery(id+"F0.wireOp",EDGE,"E71.MirrorCS");Q0=makeQuery(id+"F0.imprint","IMPRINT",FACE,{"disambiguationData":[TD([[makeQuery(id+"F0.imprint","IMPRINT",EDGE,{"derivedFrom":subQ0}),-1.0]])]});}
            var Q1;
            {var subQ0=sQuery(id+"F0.wireOp",EDGE,"E73.MirrorCS");Q1=makeQuery(id+"F0.imprint","IMPRINT",FACE,{"disambiguationData":[TD([[makeQuery(id+"F0.imprint","IMPRINT",EDGE,{"derivedFrom":subQ0}),1.0]])]});}
            var Q2;
            {var subQ1=sQuery(id+"F0.wireOp",EDGE,"E48");Q2=makeQuery(id+"F0.imprint","IMPRINT",FACE,{"disambiguationData":[TD([[makeQuery(id+"F0.imprint","IMPRINT",EDGE,{"derivedFrom":subQ1}),-1.0]])]});}
            var Q3;
            {var subQ1=sQuery(id+"F0.wireOp",EDGE,"E53.MirrorCS");Q3=makeQuery(id+"F0.imprint","IMPRINT",FACE,{"disambiguationData":[TD([[makeQuery(id+"F0.imprint","IMPRINT",EDGE,{"derivedFrom":subQ1}),1.0]])]});}
            var Q4;
            {var subQ1=sQuery(id+"F0.wireOp",EDGE,"E63.MirrorCS");Q4=makeQuery(id+"F0.imprint","IMPRINT",FACE,{"disambiguationData":[TD([[makeQuery(id+"F0.imprint","IMPRINT",EDGE,{"derivedFrom":subQ1}),-1.0]])]});}
            var Q5;
            {var subQ6=sQuery(id+"F0.wireOp",EDGE,"E61.MirrorCS");Q5=makeQuery(id+"F0.imprint","IMPRINT",FACE,{"disambiguationData":[TD([[makeQuery(id+"F0.imprint","IMPRINT",EDGE,{"derivedFrom":subQ6}),1.0]])]});}
            extrude(context, id + "F2", {"entities" : qUnion([Q0, Q1, Q2, Q3, Q4, Q5]), "operationType" : NewBodyOperationType.ADD, "depth" : 2.54 * mm});
        }
        {
            var Q0;
            {var subQ3=sQuery(id+"F0.wireOp",EDGE,"E73.MirrorCS");Q0=makeQuery(id+"F0.imprint","IMPRINT",FACE,{"disambiguationData":[TD([[makeQuery(id+"F0.imprint","IMPRINT",EDGE,{"derivedFrom":subQ3}),-1.0]])]});}
            var Q1;
            {var subQ3=sQuery(id+"F0.wireOp",EDGE,"E3");var subQ5=sQuery(id+"F0.wireOp",EDGE,"E12.MirrorCS");var subQ7=makeQuery(id+"F0.imprint","INTERSECT",VERTEX,{"derivedFrom":[subQ3,subQ5]});Q1=makeQuery(id+"F0.imprint","IMPRINT",FACE,{"disambiguationData":[TD([[makeQuery(id+"F0.imprint","IMPRINT",EDGE,{"disambiguationData":[TD([[subQ7,-1.0]])],"derivedFrom":subQ3}),1.0]])]});}
            var Q2;
            {var subQ4=sQuery(id+"F0.wireOp",EDGE,"E37");Q2=makeQuery(id+"F0.imprint","IMPRINT",FACE,{"disambiguationData":[TD([[makeQuery(id+"F0.imprint","IMPRINT",EDGE,{"derivedFrom":subQ4}),1.0]])]});}
            var Q3;
            {var subQ6=sQuery(id+"F0.wireOp",EDGE,"E37");Q3=makeQuery(id+"F0.imprint","IMPRINT",FACE,{"disambiguationData":[TD([[makeQuery(id+"F0.imprint","IMPRINT",EDGE,{"derivedFrom":subQ6}),-1.0]])]});}
            var Q4;
            {var subQ3=sQuery(id+"F0.wireOp",EDGE,"E7");var subQ5=sQuery(id+"F0.wireOp",EDGE,"E3");var subQ7=makeQuery(id+"F0.imprint","INTERSECT",VERTEX,{"derivedFrom":[subQ5,subQ3]});Q4=makeQuery(id+"F0.imprint","IMPRINT",FACE,{"disambiguationData":[TD([[makeQuery(id+"F0.imprint","IMPRINT",EDGE,{"disambiguationData":[TD([[subQ7,1.0]])],"derivedFrom":subQ5}),1.0]])]});}
            var Q5;
            {var subQ6=sQuery(id+"F0.wireOp",EDGE,"E61.MirrorCS");Q5=makeQuery(id+"F0.imprint","IMPRINT",FACE,{"disambiguationData":[TD([[makeQuery(id+"F0.imprint","IMPRINT",EDGE,{"derivedFrom":subQ6}),-1.0]])]});}
            var Q6;
            {var subQ3=sQuery(id+"F0.wireOp",EDGE,"E11");var subQ5=sQuery(id+"F0.wireOp",EDGE,"E3");var subQ7=makeQuery(id+"F0.imprint","INTERSECT",VERTEX,{"derivedFrom":[subQ5,subQ3]});Q6=makeQuery(id+"F0.imprint","IMPRINT",FACE,{"disambiguationData":[TD([[makeQuery(id+"F0.imprint","IMPRINT",EDGE,{"disambiguationData":[TD([[subQ7,1.0]])],"derivedFrom":subQ5}),1.0]])]});}
            extrude(context, id + "F3", {"entities" : qUnion([Q0, Q1, Q2, Q3, Q4, Q5, Q6]), "operationType" : NewBodyOperationType.ADD, "depth" : 5.08 * mm});
        }
        {
            var Q0;
            {var subQ6=sQuery(id+"F0.wireOp",EDGE,"E71.MirrorCS");Q0=makeQuery(id+"F0.imprint","IMPRINT",FACE,{"disambiguationData":[TD([[makeQuery(id+"F0.imprint","IMPRINT",EDGE,{"derivedFrom":subQ6}),1.0]])]});}
            var Q1;
            {var subQ3=sQuery(id+"F0.wireOp",EDGE,"E0.MirrorCS");var subQ5=sQuery(id+"F0.wireOp",EDGE,"E3");var subQ7=makeQuery(id+"F0.imprint","INTERSECT",VERTEX,{"derivedFrom":[subQ3,subQ5]});Q1=makeQuery(id+"F0.imprint","IMPRINT",FACE,{"disambiguationData":[TD([[makeQuery(id+"F0.imprint","IMPRINT",EDGE,{"disambiguationData":[TD([[subQ7,1.0]])],"derivedFrom":subQ3}),1.0]])]});}
            var Q2;
            {var subQ6=sQuery(id+"F0.wireOp",EDGE,"E63.MirrorCS");Q2=makeQuery(id+"F0.imprint","IMPRINT",FACE,{"disambiguationData":[TD([[makeQuery(id+"F0.imprint","IMPRINT",EDGE,{"derivedFrom":subQ6}),1.0]])]});}
            var Q3;
            {var subQ3=sQuery(id+"F0.wireOp",EDGE,"E8.MirrorCS");var subQ5=sQuery(id+"F0.wireOp",EDGE,"E3");var subQ7=makeQuery(id+"F0.imprint","INTERSECT",VERTEX,{"derivedFrom":[subQ5,subQ3]});Q3=makeQuery(id+"F0.imprint","IMPRINT",FACE,{"disambiguationData":[TD([[makeQuery(id+"F0.imprint","IMPRINT",EDGE,{"disambiguationData":[TD([[subQ7,-1.0]])],"derivedFrom":subQ5}),1.0]])]});}
            var Q4;
            {var subQ3=sQuery(id+"F0.wireOp",EDGE,"E12.MirrorCS");var subQ5=sQuery(id+"F0.wireOp",EDGE,"E3");var subQ7=makeQuery(id+"F0.imprint","INTERSECT",VERTEX,{"derivedFrom":[subQ5,subQ3]});Q4=makeQuery(id+"F0.imprint","IMPRINT",FACE,{"disambiguationData":[TD([[makeQuery(id+"F0.imprint","IMPRINT",EDGE,{"disambiguationData":[TD([[subQ7,1.0]])],"derivedFrom":subQ5}),1.0]])]});}
            var Q5;
            {var subQ0=sQuery(id+"F0.wireOp",EDGE,"E35");Q5=makeQuery(id+"F0.imprint","IMPRINT",FACE,{"disambiguationData":[TD([[makeQuery(id+"F0.imprint","IMPRINT",EDGE,{"derivedFrom":subQ0}),1.0]])]});}
            var Q6;
            {var subQ9=sQuery(id+"F0.wireOp",EDGE,"E35");Q6=makeQuery(id+"F0.imprint","IMPRINT",FACE,{"disambiguationData":[TD([[makeQuery(id+"F0.imprint","IMPRINT",EDGE,{"derivedFrom":subQ9}),-1.0]])]});}
            extrude(context, id + "F4", {"entities" : qUnion([Q0, Q1, Q2, Q3, Q4, Q5, Q6]), "operationType" : NewBodyOperationType.ADD, "depth" : 7.62 * mm});
        }
        {
            var Q0;
            {var subQ6=sQuery(id+"F0.wireOp",EDGE,"E39");Q0=makeQuery(id+"F0.imprint","IMPRINT",FACE,{"disambiguationData":[TD([[makeQuery(id+"F0.imprint","IMPRINT",EDGE,{"derivedFrom":subQ6}),1.0]])]});}
            extrude(context, id + "F5", {"entities" : qUnion([Q0]), "operationType" : NewBodyOperationType.ADD, "depth" : 12.7 * mm});
        }
        {
            var Q0;
            {var subQ4=sQuery(id+"F0.wireOp",EDGE,"E41");Q0=makeQuery(id+"F0.imprint","IMPRINT",FACE,{"disambiguationData":[TD([[makeQuery(id+"F0.imprint","IMPRINT",EDGE,{"derivedFrom":subQ4}),1.0]])]});}
            extrude(context, id + "F6", {"entities" : qUnion([Q0]), "operationType" : NewBodyOperationType.ADD, "depth" : 10.16 * mm});
        }
        {
            var Q0;
            {var subQ0=sQuery(id+"F0.wireOp",EDGE,"E67.MirrorCS");var subQ3=sQuery(id+"F0.wireOp",EDGE,"E11");var subQ4=makeQuery(id+"F0.imprint","INTERSECT",VERTEX,{"derivedFrom":[subQ3,subQ0]});Q0=makeQuery(id+"F0.imprint","IMPRINT",FACE,{"disambiguationData":[TD([[makeQuery(id+"F0.imprint","IMPRINT",EDGE,{"disambiguationData":[TD([[subQ4,-1.0]])],"derivedFrom":subQ3}),1.0]])]});}
            var Q1;
            {var subQ3=sQuery(id+"F0.wireOp",EDGE,"E11");var subQ8=makeQuery(id+"F0.imprint","INTERSECT",VERTEX,{"derivedFrom":[subQ3,sQuery(id+"F0.wireOp",EDGE,"E57.MirrorCS")]});Q1=makeQuery(id+"F0.imprint","IMPRINT",FACE,{"disambiguationData":[TD([[makeQuery(id+"F0.imprint","IMPRINT",EDGE,{"disambiguationData":[TD([[subQ8,-1.0]])],"derivedFrom":subQ3}),1.0]])]});}
            var Q2;
            {var subQ3=sQuery(id+"F0.wireOp",EDGE,"E14.MirrorCS");var subQ8=makeQuery(id+"F0.imprint","INTERSECT",VERTEX,{"derivedFrom":[subQ3,sQuery(id+"F0.wireOp",EDGE,"E25")]});Q2=makeQuery(id+"F0.imprint","IMPRINT",FACE,{"disambiguationData":[TD([[makeQuery(id+"F0.imprint","IMPRINT",EDGE,{"disambiguationData":[TD([[subQ8,-1.0]])],"derivedFrom":subQ3}),-1.0]])]});}
            var Q3;
            {var subQ0=sQuery(id+"F0.wireOp",EDGE,"E70.MirrorCS");var subQ3=sQuery(id+"F0.wireOp",EDGE,"E14.MirrorCS");var subQ4=makeQuery(id+"F0.imprint","INTERSECT",VERTEX,{"derivedFrom":[subQ3,subQ0]});Q3=makeQuery(id+"F0.imprint","IMPRINT",FACE,{"disambiguationData":[TD([[makeQuery(id+"F0.imprint","IMPRINT",EDGE,{"disambiguationData":[TD([[subQ4,-1.0]])],"derivedFrom":subQ3}),-1.0]])]});}
            var Q4;
            {var subQ1=sQuery(id+"F0.wireOp",EDGE,"E14.MirrorCS");var subQ5=sQuery(id+"F0.wireOp",EDGE,"E70.MirrorCS");var subQ6=makeQuery(id+"F0.imprint","INTERSECT",VERTEX,{"derivedFrom":[subQ1,subQ5]});Q4=makeQuery(id+"F0.imprint","IMPRINT",FACE,{"disambiguationData":[TD([[makeQuery(id+"F0.imprint","IMPRINT",EDGE,{"disambiguationData":[TD([[subQ6,-1.0]])],"derivedFrom":subQ1}),1.0]])]});}
            var Q5;
            {var subQ0=sQuery(id+"F0.wireOp",EDGE,"E47");var subQ3=sQuery(id+"F0.wireOp",EDGE,"E18.MirrorCS");var subQ4=makeQuery(id+"F0.imprint","INTERSECT",VERTEX,{"derivedFrom":[subQ3,subQ0]});Q5=makeQuery(id+"F0.imprint","IMPRINT",FACE,{"disambiguationData":[TD([[makeQuery(id+"F0.imprint","IMPRINT",EDGE,{"disambiguationData":[TD([[subQ4,-1.0]])],"derivedFrom":subQ3}),-1.0]])]});}
            var Q6;
            {var subQ0=sQuery(id+"F0.wireOp",EDGE,"E47");var subQ3=sQuery(id+"F0.wireOp",EDGE,"E18.MirrorCS");var subQ4=makeQuery(id+"F0.imprint","INTERSECT",VERTEX,{"derivedFrom":[subQ3,subQ0]});Q6=makeQuery(id+"F0.imprint","IMPRINT",FACE,{"disambiguationData":[TD([[makeQuery(id+"F0.imprint","IMPRINT",EDGE,{"disambiguationData":[TD([[subQ4,-1.0]])],"derivedFrom":subQ3}),1.0]])]});}
            var Q7;
            {var subQ1=sQuery(id+"F0.wireOp",EDGE,"E52.MirrorCS");var subQ3=sQuery(id+"F0.wireOp",EDGE,"E8.MirrorCS");var subQ5=makeQuery(id+"F0.imprint","INTERSECT",VERTEX,{"derivedFrom":[subQ3,subQ1]});Q7=makeQuery(id+"F0.imprint","IMPRINT",FACE,{"disambiguationData":[TD([[makeQuery(id+"F0.imprint","IMPRINT",EDGE,{"disambiguationData":[TD([[subQ5,-1.0]])],"derivedFrom":subQ3}),-1.0]])]});}
            var Q8;
            {var subQ0=sQuery(id+"F0.wireOp",EDGE,"E58.MirrorCS");var subQ3=sQuery(id+"F0.wireOp",EDGE,"E7");var subQ4=makeQuery(id+"F0.imprint","INTERSECT",VERTEX,{"derivedFrom":[subQ3,subQ0]});Q8=makeQuery(id+"F0.imprint","IMPRINT",FACE,{"disambiguationData":[TD([[makeQuery(id+"F0.imprint","IMPRINT",EDGE,{"disambiguationData":[TD([[subQ4,-1.0]])],"derivedFrom":subQ3}),1.0]])]});}
            var Q9;
            {var subQ5=sQuery(id+"F0.wireOp",EDGE,"E51.MirrorCS");Q9=makeQuery(id+"F0.imprint","IMPRINT",FACE,{"disambiguationData":[TD([[makeQuery(id+"F0.imprint","IMPRINT",EDGE,{"derivedFrom":subQ5}),1.0]])]});}
            var Q10;
            {var subQ3=sQuery(id+"F0.wireOp",EDGE,"E0.MirrorCS");var subQ5=makeQuery(id+"F0.imprint","INTERSECT",VERTEX,{"derivedFrom":[subQ3,sQuery(id+"F0.wireOp",EDGE,"E67.MirrorCS")]});Q10=makeQuery(id+"F0.imprint","IMPRINT",FACE,{"disambiguationData":[TD([[makeQuery(id+"F0.imprint","IMPRINT",EDGE,{"disambiguationData":[TD([[subQ5,-1.0]])],"derivedFrom":subQ3}),-1.0]])]});}
            var Q11;
            {var subQ0=sQuery(id+"F0.wireOp",EDGE,"E57.MirrorCS");var subQ3=sQuery(id+"F0.wireOp",EDGE,"E0.MirrorCS");var subQ4=makeQuery(id+"F0.imprint","INTERSECT",VERTEX,{"derivedFrom":[subQ3,subQ0]});Q11=makeQuery(id+"F0.imprint","IMPRINT",FACE,{"disambiguationData":[TD([[makeQuery(id+"F0.imprint","IMPRINT",EDGE,{"disambiguationData":[TD([[subQ4,-1.0]])],"derivedFrom":subQ3}),-1.0]])]});}
            var Q12;
            {var subQ0=sQuery(id+"F0.wireOp",EDGE,"E57.MirrorCS");var subQ3=sQuery(id+"F0.wireOp",EDGE,"E0.MirrorCS");var subQ4=makeQuery(id+"F0.imprint","INTERSECT",VERTEX,{"derivedFrom":[subQ3,subQ0]});Q12=makeQuery(id+"F0.imprint","IMPRINT",FACE,{"disambiguationData":[TD([[makeQuery(id+"F0.imprint","IMPRINT",EDGE,{"disambiguationData":[TD([[subQ4,-1.0]])],"derivedFrom":subQ3}),1.0]])]});}
            var Q13;
            {var subQ0=sQuery(id+"F0.wireOp",EDGE,"E67.MirrorCS");var subQ3=sQuery(id+"F0.wireOp",EDGE,"E11");var subQ4=makeQuery(id+"F0.imprint","INTERSECT",VERTEX,{"derivedFrom":[subQ3,subQ0]});Q13=makeQuery(id+"F0.imprint","IMPRINT",FACE,{"disambiguationData":[TD([[makeQuery(id+"F0.imprint","IMPRINT",EDGE,{"disambiguationData":[TD([[subQ4,-1.0]])],"derivedFrom":subQ3}),-1.0]])]});}
            var Q14;
            {var subQ0=sQuery(id+"F0.wireOp",EDGE,"E57.MirrorCS");var subQ3=sQuery(id+"F0.wireOp",EDGE,"E11");var subQ4=makeQuery(id+"F0.imprint","INTERSECT",VERTEX,{"derivedFrom":[subQ3,subQ0]});Q14=makeQuery(id+"F0.imprint","IMPRINT",FACE,{"disambiguationData":[TD([[makeQuery(id+"F0.imprint","IMPRINT",EDGE,{"disambiguationData":[TD([[subQ4,1.0]])],"derivedFrom":subQ3}),-1.0]])]});}
            var Q15;
            {var subQ0=sQuery(id+"F0.wireOp",EDGE,"E67.MirrorCS");var subQ3=sQuery(id+"F0.wireOp",EDGE,"E0.MirrorCS");var subQ4=makeQuery(id+"F0.imprint","INTERSECT",VERTEX,{"derivedFrom":[subQ3,subQ0]});Q15=makeQuery(id+"F0.imprint","IMPRINT",FACE,{"disambiguationData":[TD([[makeQuery(id+"F0.imprint","IMPRINT",EDGE,{"disambiguationData":[TD([[subQ4,1.0]])],"derivedFrom":subQ3}),1.0]])]});}
            var Q16;
            {var subQ0=sQuery(id+"F0.wireOp",EDGE,"E67.MirrorCS");var subQ3=sQuery(id+"F0.wireOp",EDGE,"E0.MirrorCS");var subQ4=makeQuery(id+"F0.imprint","INTERSECT",VERTEX,{"derivedFrom":[subQ3,subQ0]});Q16=makeQuery(id+"F0.imprint","IMPRINT",FACE,{"disambiguationData":[TD([[makeQuery(id+"F0.imprint","IMPRINT",EDGE,{"disambiguationData":[TD([[subQ4,-1.0]])],"derivedFrom":subQ3}),1.0]])]});}
            var Q17;
            {var subQ1=sQuery(id+"F0.wireOp",EDGE,"E57.MirrorCS");var subQ3=sQuery(id+"F0.wireOp",EDGE,"E11");var subQ5=makeQuery(id+"F0.imprint","INTERSECT",VERTEX,{"derivedFrom":[subQ3,subQ1]});Q17=makeQuery(id+"F0.imprint","IMPRINT",FACE,{"disambiguationData":[TD([[makeQuery(id+"F0.imprint","IMPRINT",EDGE,{"disambiguationData":[TD([[subQ5,-1.0]])],"derivedFrom":subQ3}),-1.0]])]});}
            var Q18;
            {var subQ1=sQuery(id+"F0.wireOp",EDGE,"E47");var subQ3=sQuery(id+"F0.wireOp",EDGE,"E14.MirrorCS");var subQ5=makeQuery(id+"F0.imprint","INTERSECT",VERTEX,{"derivedFrom":[subQ3,subQ1]});Q18=makeQuery(id+"F0.imprint","IMPRINT",FACE,{"disambiguationData":[TD([[makeQuery(id+"F0.imprint","IMPRINT",EDGE,{"disambiguationData":[TD([[subQ5,-1.0]])],"derivedFrom":subQ3}),1.0]])]});}
            var Q19;
            {var subQ0=sQuery(id+"F0.wireOp",EDGE,"E58.MirrorCS");var subQ3=sQuery(id+"F0.wireOp",EDGE,"E7");var subQ4=makeQuery(id+"F0.imprint","INTERSECT",VERTEX,{"derivedFrom":[subQ3,subQ0]});Q19=makeQuery(id+"F0.imprint","IMPRINT",FACE,{"disambiguationData":[TD([[makeQuery(id+"F0.imprint","IMPRINT",EDGE,{"disambiguationData":[TD([[subQ4,-1.0]])],"derivedFrom":subQ3}),-1.0]])]});}
            var Q20;
            {var subQ3=sQuery(id+"F0.wireOp",EDGE,"E8.MirrorCS");var subQ5=sQuery(id+"F0.wireOp",EDGE,"E52.MirrorCS");var subQ7=makeQuery(id+"F0.imprint","INTERSECT",VERTEX,{"derivedFrom":[subQ3,subQ5]});Q20=makeQuery(id+"F0.imprint","IMPRINT",FACE,{"disambiguationData":[TD([[makeQuery(id+"F0.imprint","IMPRINT",EDGE,{"disambiguationData":[TD([[subQ7,-1.0]])],"derivedFrom":subQ3}),1.0]])]});}
            var Q21;
            {var subQ1=sQuery(id+"F0.wireOp",EDGE,"E52.MirrorCS");var subQ3=sQuery(id+"F0.wireOp",EDGE,"E7");var subQ5=makeQuery(id+"F0.imprint","INTERSECT",VERTEX,{"derivedFrom":[subQ3,subQ1]});Q21=makeQuery(id+"F0.imprint","IMPRINT",FACE,{"disambiguationData":[TD([[makeQuery(id+"F0.imprint","IMPRINT",EDGE,{"disambiguationData":[TD([[subQ5,-1.0]])],"derivedFrom":subQ3}),-1.0]])]});}
            var Q22;
            {var subQ0=sQuery(id+"F0.wireOp",EDGE,"E23.MirrorCS");var subQ3=sQuery(id+"F0.wireOp",EDGE,"E8.MirrorCS");var subQ4=makeQuery(id+"F0.imprint","INTERSECT",VERTEX,{"derivedFrom":[subQ3,subQ0]});Q22=makeQuery(id+"F0.imprint","IMPRINT",FACE,{"disambiguationData":[TD([[makeQuery(id+"F0.imprint","IMPRINT",EDGE,{"disambiguationData":[TD([[subQ4,-1.0]])],"derivedFrom":subQ3}),-1.0]])]});}
            var Q23;
            {var subQ3=sQuery(id+"F0.wireOp",EDGE,"E8.MirrorCS");var subQ5=sQuery(id+"F0.wireOp",EDGE,"E21.MirrorCS");var subQ7=makeQuery(id+"F0.imprint","INTERSECT",VERTEX,{"derivedFrom":[subQ3,subQ5]});Q23=makeQuery(id+"F0.imprint","IMPRINT",FACE,{"disambiguationData":[TD([[makeQuery(id+"F0.imprint","IMPRINT",EDGE,{"disambiguationData":[TD([[subQ7,-1.0]])],"derivedFrom":subQ3}),-1.0]])]});}
            var Q24;
            {var subQ3=sQuery(id+"F0.wireOp",EDGE,"E8.MirrorCS");var subQ5=makeQuery(id+"F0.imprint","INTERSECT",VERTEX,{"derivedFrom":[subQ3,sQuery(id+"F0.wireOp",EDGE,"E58.MirrorCS")]});Q24=makeQuery(id+"F0.imprint","IMPRINT",FACE,{"disambiguationData":[TD([[makeQuery(id+"F0.imprint","IMPRINT",EDGE,{"disambiguationData":[TD([[subQ5,-1.0]])],"derivedFrom":subQ3}),-1.0]])]});}
            var Q25;
            {var subQ3=sQuery(id+"F0.wireOp",EDGE,"E18.MirrorCS");var subQ7=makeQuery(id+"F0.imprint","INTERSECT",VERTEX,{"derivedFrom":[subQ3,sQuery(id+"F0.wireOp",EDGE,"E70.MirrorCS")]});Q25=makeQuery(id+"F0.imprint","IMPRINT",FACE,{"disambiguationData":[TD([[makeQuery(id+"F0.imprint","IMPRINT",EDGE,{"disambiguationData":[TD([[subQ7,-1.0]])],"derivedFrom":subQ3}),1.0]])]});}
            var Q26;
            {var subQ0=sQuery(id+"F0.wireOp",EDGE,"E24");var subQ3=sQuery(id+"F0.wireOp",EDGE,"E18.MirrorCS");var subQ4=makeQuery(id+"F0.imprint","INTERSECT",VERTEX,{"derivedFrom":[subQ3,subQ0]});Q26=makeQuery(id+"F0.imprint","IMPRINT",FACE,{"disambiguationData":[TD([[makeQuery(id+"F0.imprint","IMPRINT",EDGE,{"disambiguationData":[TD([[subQ4,-1.0]])],"derivedFrom":subQ3}),1.0]])]});}
            var Q27;
            {var subQ3=sQuery(id+"F0.wireOp",EDGE,"E18.MirrorCS");var subQ5=sQuery(id+"F0.wireOp",EDGE,"E25");var subQ7=makeQuery(id+"F0.imprint","INTERSECT",VERTEX,{"derivedFrom":[subQ3,subQ5]});Q27=makeQuery(id+"F0.imprint","IMPRINT",FACE,{"disambiguationData":[TD([[makeQuery(id+"F0.imprint","IMPRINT",EDGE,{"disambiguationData":[TD([[subQ7,-1.0]])],"derivedFrom":subQ3}),1.0]])]});}
            var Q28;
            {var subQ1=sQuery(id+"F0.wireOp",EDGE,"E24");var subQ7=sQuery(id+"F0.wireOp",EDGE,"E12.MirrorCS");var subQ9=makeQuery(id+"F0.imprint","INTERSECT",VERTEX,{"derivedFrom":[subQ7,subQ1]});Q28=makeQuery(id+"F0.imprint","IMPRINT",FACE,{"disambiguationData":[TD([[makeQuery(id+"F0.imprint","IMPRINT",EDGE,{"disambiguationData":[TD([[subQ9,-1.0]])],"derivedFrom":subQ1}),1.0]])]});}
            var Q29;
            {var subQ3=sQuery(id+"F0.wireOp",EDGE,"E24");var subQ5=sQuery(id+"F0.wireOp",EDGE,"E12.MirrorCS");var subQ7=makeQuery(id+"F0.imprint","INTERSECT",VERTEX,{"derivedFrom":[subQ5,subQ3]});Q29=makeQuery(id+"F0.imprint","IMPRINT",FACE,{"disambiguationData":[TD([[makeQuery(id+"F0.imprint","IMPRINT",EDGE,{"disambiguationData":[TD([[subQ7,-1.0]])],"derivedFrom":subQ5}),1.0]])]});}
            var Q30;
            {var subQ3=sQuery(id+"F0.wireOp",EDGE,"E24");var subQ5=sQuery(id+"F0.wireOp",EDGE,"E18.MirrorCS");var subQ6=makeQuery(id+"F0.imprint","INTERSECT",VERTEX,{"derivedFrom":[subQ5,subQ3]});Q30=makeQuery(id+"F0.imprint","IMPRINT",FACE,{"disambiguationData":[TD([[makeQuery(id+"F0.imprint","IMPRINT",EDGE,{"disambiguationData":[TD([[subQ6,-1.0]])],"derivedFrom":subQ5}),-1.0]])]});}
            var Q31;
            {var subQ3=sQuery(id+"F0.wireOp",EDGE,"E25");var subQ5=sQuery(id+"F0.wireOp",EDGE,"E18.MirrorCS");var subQ7=makeQuery(id+"F0.imprint","INTERSECT",VERTEX,{"derivedFrom":[subQ5,subQ3]});Q31=makeQuery(id+"F0.imprint","IMPRINT",FACE,{"disambiguationData":[TD([[makeQuery(id+"F0.imprint","IMPRINT",EDGE,{"disambiguationData":[TD([[subQ7,-1.0]])],"derivedFrom":subQ5}),-1.0]])]});}
            var Q32;
            {var subQ0=sQuery(id+"F0.wireOp",EDGE,"E25");var subQ3=sQuery(id+"F0.wireOp",EDGE,"E14.MirrorCS");var subQ4=makeQuery(id+"F0.imprint","INTERSECT",VERTEX,{"derivedFrom":[subQ3,subQ0]});Q32=makeQuery(id+"F0.imprint","IMPRINT",FACE,{"disambiguationData":[TD([[makeQuery(id+"F0.imprint","IMPRINT",EDGE,{"disambiguationData":[TD([[subQ4,-1.0]])],"derivedFrom":subQ3}),1.0]])]});}
            var Q33;
            {var subQ1=sQuery(id+"F0.wireOp",EDGE,"E12.MirrorCS");var subQ8=makeQuery(id+"F0.imprint","INTERSECT",VERTEX,{"derivedFrom":[subQ1,sQuery(id+"F0.wireOp",EDGE,"E24")]});Q33=makeQuery(id+"F0.imprint","IMPRINT",FACE,{"disambiguationData":[TD([[makeQuery(id+"F0.imprint","IMPRINT",EDGE,{"disambiguationData":[TD([[subQ8,-1.0]])],"derivedFrom":subQ1}),-1.0]])]});}
            var Q34;
            {var subQ1=sQuery(id+"F0.wireOp",EDGE,"E12.MirrorCS");var subQ8=makeQuery(id+"F0.imprint","INTERSECT",VERTEX,{"derivedFrom":[subQ1,sQuery(id+"F0.wireOp",EDGE,"E24")]});Q34=makeQuery(id+"F0.imprint","IMPRINT",FACE,{"disambiguationData":[TD([[makeQuery(id+"F0.imprint","IMPRINT",EDGE,{"disambiguationData":[TD([[subQ8,-1.0]])],"derivedFrom":subQ1}),-1.0]])]});}
            var Q35;
            {var subQ1=sQuery(id+"F0.wireOp",EDGE,"E12.MirrorCS");var subQ3=sQuery(id+"F0.wireOp",EDGE,"E25");var subQ5=makeQuery(id+"F0.imprint","INTERSECT",VERTEX,{"derivedFrom":[subQ1,subQ3]});Q35=makeQuery(id+"F0.imprint","IMPRINT",FACE,{"disambiguationData":[TD([[makeQuery(id+"F0.imprint","IMPRINT",EDGE,{"disambiguationData":[TD([[subQ5,-1.0]])],"derivedFrom":subQ3}),-1.0]])]});}
            var Q36;
            {var subQ0=sQuery(id+"F0.wireOp",EDGE,"E70.MirrorCS");var subQ3=sQuery(id+"F0.wireOp",EDGE,"E18.MirrorCS");var subQ4=makeQuery(id+"F0.imprint","INTERSECT",VERTEX,{"derivedFrom":[subQ3,subQ0]});Q36=makeQuery(id+"F0.imprint","IMPRINT",FACE,{"disambiguationData":[TD([[makeQuery(id+"F0.imprint","IMPRINT",EDGE,{"disambiguationData":[TD([[subQ4,-1.0]])],"derivedFrom":subQ3}),-1.0]])]});}
            var Q37;
            {var subQ5=sQuery(id+"F0.wireOp",EDGE,"E17");var subQ7=sQuery(id+"F0.wireOp",EDGE,"E21.MirrorCS");var subQ8=makeQuery(id+"F0.imprint","INTERSECT",VERTEX,{"derivedFrom":[subQ5,subQ7]});Q37=makeQuery(id+"F0.imprint","IMPRINT",FACE,{"disambiguationData":[TD([[makeQuery(id+"F0.imprint","IMPRINT",EDGE,{"disambiguationData":[TD([[subQ8,-1.0]])],"derivedFrom":subQ7}),-1.0]])]});}
            var Q38;
            {var subQ1=sQuery(id+"F0.wireOp",EDGE,"E17");var subQ8=makeQuery(id+"F0.imprint","INTERSECT",VERTEX,{"derivedFrom":[subQ1,sQuery(id+"F0.wireOp",EDGE,"E21.MirrorCS")]});Q38=makeQuery(id+"F0.imprint","IMPRINT",FACE,{"disambiguationData":[TD([[makeQuery(id+"F0.imprint","IMPRINT",EDGE,{"disambiguationData":[TD([[subQ8,-1.0]])],"derivedFrom":subQ1}),1.0]])]});}
            var Q39;
            {var subQ3=sQuery(id+"F0.wireOp",EDGE,"E7");var subQ5=sQuery(id+"F0.wireOp",EDGE,"E23.MirrorCS");var subQ7=makeQuery(id+"F0.imprint","INTERSECT",VERTEX,{"derivedFrom":[subQ3,subQ5]});Q39=makeQuery(id+"F0.imprint","IMPRINT",FACE,{"disambiguationData":[TD([[makeQuery(id+"F0.imprint","IMPRINT",EDGE,{"disambiguationData":[TD([[subQ7,-1.0]])],"derivedFrom":subQ3}),-1.0]])]});}
            var Q40;
            {var subQ3=sQuery(id+"F0.wireOp",EDGE,"E51.MirrorCS");Q40=makeQuery(id+"F0.imprint","IMPRINT",FACE,{"disambiguationData":[TD([[makeQuery(id+"F0.imprint","IMPRINT",EDGE,{"derivedFrom":subQ3}),-1.0]])]});}
            var Q41;
            {var subQ3=sQuery(id+"F0.wireOp",EDGE,"E23.MirrorCS");var subQ5=sQuery(id+"F0.wireOp",EDGE,"E8.MirrorCS");var subQ6=makeQuery(id+"F0.imprint","INTERSECT",VERTEX,{"derivedFrom":[subQ5,subQ3]});Q41=makeQuery(id+"F0.imprint","IMPRINT",FACE,{"disambiguationData":[TD([[makeQuery(id+"F0.imprint","IMPRINT",EDGE,{"disambiguationData":[TD([[subQ6,-1.0]])],"derivedFrom":subQ5}),1.0]])]});}
            var Q42;
            {var subQ1=sQuery(id+"F0.wireOp",EDGE,"E17");var subQ3=sQuery(id+"F0.wireOp",EDGE,"E23.MirrorCS");var subQ5=makeQuery(id+"F0.imprint","INTERSECT",VERTEX,{"derivedFrom":[subQ1,subQ3]});Q42=makeQuery(id+"F0.imprint","IMPRINT",FACE,{"disambiguationData":[TD([[makeQuery(id+"F0.imprint","IMPRINT",EDGE,{"disambiguationData":[TD([[subQ5,-1.0]])],"derivedFrom":subQ3}),1.0]])]});}
            var Q43;
            {var subQ3=sQuery(id+"F0.wireOp",EDGE,"E21.MirrorCS");var subQ5=sQuery(id+"F0.wireOp",EDGE,"E17");var subQ7=makeQuery(id+"F0.imprint","INTERSECT",VERTEX,{"derivedFrom":[subQ5,subQ3]});Q43=makeQuery(id+"F0.imprint","IMPRINT",FACE,{"disambiguationData":[TD([[makeQuery(id+"F0.imprint","IMPRINT",EDGE,{"disambiguationData":[TD([[subQ7,-1.0]])],"derivedFrom":subQ5}),-1.0]])]});}
            var Q44;
            {var subQ3=sQuery(id+"F0.wireOp",EDGE,"E21.MirrorCS");var subQ5=sQuery(id+"F0.wireOp",EDGE,"E8.MirrorCS");var subQ7=makeQuery(id+"F0.imprint","INTERSECT",VERTEX,{"derivedFrom":[subQ5,subQ3]});Q44=makeQuery(id+"F0.imprint","IMPRINT",FACE,{"disambiguationData":[TD([[makeQuery(id+"F0.imprint","IMPRINT",EDGE,{"disambiguationData":[TD([[subQ7,-1.0]])],"derivedFrom":subQ5}),1.0]])]});}
            var Q45;
            {var subQ0=sQuery(id+"F0.wireOp",EDGE,"E58.MirrorCS");var subQ3=sQuery(id+"F0.wireOp",EDGE,"E8.MirrorCS");var subQ4=makeQuery(id+"F0.imprint","INTERSECT",VERTEX,{"derivedFrom":[subQ3,subQ0]});Q45=makeQuery(id+"F0.imprint","IMPRINT",FACE,{"disambiguationData":[TD([[makeQuery(id+"F0.imprint","IMPRINT",EDGE,{"disambiguationData":[TD([[subQ4,-1.0]])],"derivedFrom":subQ3}),1.0]])]});}
            extrude(context, id + "F7", {"entities" : qUnion([Q0, Q1, Q2, Q3, Q4, Q5, Q6, Q7, Q8, Q9, Q10, Q11, Q12, Q13, Q14, Q15, Q16, Q17, Q18, Q19, Q20, Q21, Q22, Q23, Q24, Q25, Q26, Q27, Q28, Q29, Q30, Q31, Q32, Q33, Q34, Q35, Q36, Q37, Q38, Q39, Q40, Q41, Q42, Q43, Q44, Q45]), "operationType" : NewBodyOperationType.ADD, "depth" : 15.24 * mm});
        }
    });
